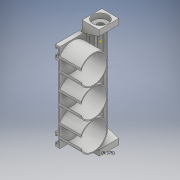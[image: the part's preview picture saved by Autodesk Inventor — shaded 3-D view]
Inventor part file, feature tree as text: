
AUTODESK INVENTOR PART (.ipt)
format: ipt  version: 2018 (Build 220112000, 112)  size: 431,104 bytes
history: native  units: mm
features: sketch x28, extrude x18, fillet x3, chamfer x2
ambient origin geometry x8: Origin, YZ Plane, XZ Plane, XY Plane, X Axis, Y Axis, Z Axis, Center Point
bodies: Solid1 (feature_tree)
feature tree (51):
  extrude  "Extrusion1"  Depth=125.0mm
  extrude  "Extrusion2"  Depth=15.0mm
  extrude  "Extrusion3"  Depth=22.0mm TaperAngle=0.0deg
  extrude  "Extrusion4"  Depth=22.0mm TaperAngle=0.0deg
  extrude  "Extrusion5"  Depth=155.0mm TaperAngle=0.0deg
  chamfer  "Chamfer1"  Distance=7.1mm
  sketch  "Sketch6"  dims[d16=22.0mm d17=7.1mm d18=0.0mm d19=7.0mm d20=2.0mm d21=12.61873mm]
  chamfer  "Chamfer2"  Distance=7.0mm
  sketch  "Sketch7"  dims[d22=7.0mm d23=2.0mm d24=12.61873mm d25=8.0mm]
  sketch  "Sketch8"  dims[d26=2.0mm d27=0.0mm d28=8.0mm]
  sketch  "Sketch9"  dims[d29=2.0mm d30=0.0mm d31=2.0mm d32=0.0mm]
  extrude  "Extrusion6"  Depth=8.0mm
  extrude  "Extrusion7"  Depth=8.0mm
  extrude  "Extrusion8"  Depth=2.0mm TaperAngle=0.0deg
  extrude  "Extrusion9"  Depth=2.0mm
  sketch  "Sketch13"  dims[d45=2.0mm d46=38.0mm]
  sketch  "Sketch14"  dims[d47=2.0mm d48=0.0mm d49=38.0mm]
  extrude  "Extrusion10"  Depth=2.0mm
  sketch  "Sketch16"  dims[d53=38.0mm d54=40.75mm]
  extrude  "Extrusion11"  Depth=7.0mm TaperAngle=0.0deg
  fillet  "Fillet1"  Radius=2.0mm
  fillet  "Fillet2"  Radius=2.0mm
  extrude  "Extrusion12"  Depth=2.0mm
  extrude  "Extrusion13"  Depth=2.0mm
  extrude  "Extrusion14"  Depth=21.75mm
  sketch  "Sketch21"  dims[d66=3.0mm]
  extrude  "Extrusion15"  Depth=40.75mm
  extrude  "Extrusion16"  Depth=40.75mm
  sketch  "Sketch24"  dims[d69=3.1mm d70=0.0mm]
  sketch  "Sketch25"  dims[d71=2.0mm]
  extrude  "Extrusion17"  Depth=32.0mm TaperAngle=0.0deg
  extrude  "Extrusion18"  Depth=3.0mm
  sketch  "Sketch28"  dims[d75=5.0mm d76=5.0mm d77=5.0mm d78=5.0mm d79=1.0mm d80=0.0mm d81=9.375mm d82=2.0mm]
  fillet  "Fillet3"  Radius=3.0mm
  sketch  "Sketch1"  dims[d0=24.0mm d1=125.0mm]
  sketch  "Sketch2"  dims[d2=2.0mm d3=0.0mm d4=15.0mm]
  sketch  "Sketch3"  dims[d5=15.0mm d6=22.0mm d7=2.0mm d8=0.0mm d9=0.0mm]
  sketch  "Sketch4"  dims[d10=22.0mm d11=7.1mm d12=0.0mm]
  sketch  "Sketch5"  dims[d13=9.0mm d14=155.0mm d15=0.0mm]
  sketch  "Sketch10"  dims[d33=2.0mm d34=0.0mm d35=5.5mm]
  sketch  "Sketch11"  dims[d36=11.0mm d37=2.0mm]
  sketch  "Sketch12"  dims[d38=2.0mm d39=7.0mm d40=0.0mm d42=2.0mm d43=0.0mm d44=2.0mm]
  sketch  "Sketch15"  dims[d51=43.5mm d52=21.75mm]
  sketch  "Sketch17"  dims[d55=38.0mm d56=40.75mm]
  sketch  "Sketch18"  dims[d57=30.0mm d58=0.0mm d59=32.0mm d60=0.0mm]
  sketch  "Sketch19"  dims[d61=3.0mm d62=12.0mm d63=3.0mm]
  sketch  "Sketch20"  dims[d64=3.1mm d65=0.0mm]
  sketch  "Sketch22"  dims[d67=12.0mm]
  sketch  "Sketch23"  dims[d68=3.0mm]
  sketch  "Sketch26"  dims[d72=2.0mm]
  sketch  "Sketch27"  dims[d73=3.6mm d74=0.0mm]
